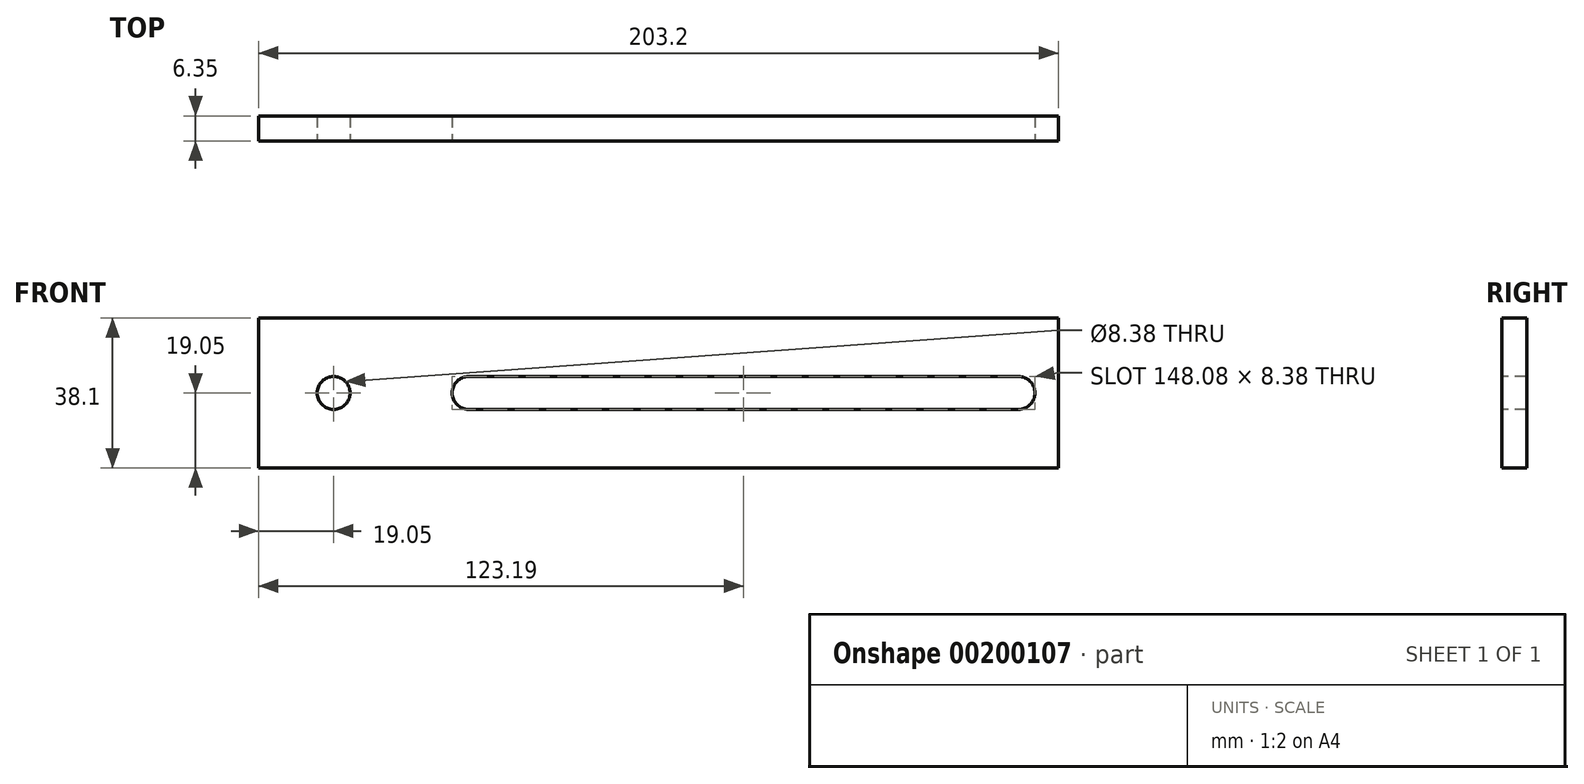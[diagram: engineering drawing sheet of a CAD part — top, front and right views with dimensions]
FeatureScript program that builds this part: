
annotation { "Feature Type Name" : "Feature", "Feature Type Description" : "" }
export const myFeature = defineFeature(function(context is Context, id is Id, definition is map)
    precondition{}
    {
        {
            var Q0;
            Q0=qCreatedBy(makeId("Front.planeOp"),FACE);
            var sketch = newSketch(context, id + "F0", { "sketchPlane" : qUnion([Q0])});
            skLineSegment(sketch, "E0.bottom", {"start": v(101.6, -19.05) * mm, "end": v(-101.6, -19.05) * mm});
            skLineSegment(sketch, "E0.top", {"start": v(101.6, 19.05) * mm, "end": v(-101.6, 19.05) * mm});
            skLineSegment(sketch, "E0.left", {"start": v(101.6, -19.05) * mm, "end": v(101.6, 19.05) * mm});
            skLineSegment(sketch, "E0.right", {"start": v(-101.6, -19.05) * mm, "end": v(-101.6, 19.05) * mm});
            skPoint(sketch, "E0.middle", {"position": v(0, 0) * mm});
            skSolve(sketch);
        }
        {
            var Q0;
            Q0=makeQuery(id+"F0.imprint","IMPRINT",FACE,{"disambiguationData":[TD([[makeQuery(id+"F0.imprint","IMPRINT",EDGE,{"derivedFrom":sQuery(id+"F0.wireOp",EDGE,"E0.bottom")}),-1.0]])]});
            extrude(context, id + "F1", {"entities" : qUnion([Q0]), "depth" : 6.35 * mm});
        }
        {
            var Q0;
            Q0=makeQuery(id+"F1.opExtrude","CAP_FACE",FACE,{"disambiguationData":[OSD([sQuery(id+"F0.wireOp",EDGE,"E0.bottom"),sQuery(id+"F0.wireOp",EDGE,"E0.top"),sQuery(id+"F0.wireOp",EDGE,"E0.left"),sQuery(id+"F0.wireOp",EDGE,"E0.right")])],"isStart":false});
            var sketch = newSketch(context, id + "F2", { "sketchPlane" : qUnion([Q0])});
            skPoint(sketch, "E1.endSnap0", {"position": v(-101.6, 0) * mm});
            skPoint(sketch, "E2", {"position": v(-82.55, 0) * mm});
            skCircle(sketch, "E3", {"center": v(-82.55, 0) * mm, "radius": 4.2 * mm});
            skSolve(sketch);
        }
        {
            var Q0;
            Q0=makeQuery(id+"F2.imprint","IMPRINT",FACE,{"disambiguationData":[TD([[makeQuery(id+"F2.imprint","IMPRINT",EDGE,{"derivedFrom":sQuery(id+"F2.wireOp",EDGE,"E3")}),1.0]])]});
            extrude(context, id + "F3", {"entities" : qUnion([Q0]), "operationType" : NewBodyOperationType.REMOVE, "endBound" : BoundingType.UP_TO_NEXT, "oppositeDirection" : true, "depth" : 25.4 * mm});
        }
        {
            var Q0;
            Q0=makeQuery(id+"F1.opExtrude","CAP_FACE",FACE,{"disambiguationData":[OSD([sQuery(id+"F0.wireOp",EDGE,"E0.bottom"),sQuery(id+"F0.wireOp",EDGE,"E0.top"),sQuery(id+"F0.wireOp",EDGE,"E0.left"),sQuery(id+"F0.wireOp",EDGE,"E0.right")])],"isStart":false});
            var sketch = newSketch(context, id + "F4", { "sketchPlane" : qUnion([Q0])});
            skLineSegment(sketch, "E4.bottom", {"start": v(91.44, -4.2) * mm, "end": v(-48.26, -4.2) * mm});
            skLineSegment(sketch, "E4.top", {"start": v(91.44, 4.2) * mm, "end": v(-48.26, 4.2) * mm});
            skLineSegment(sketch, "E4.left", {"start": v(91.44, -4.2) * mm, "end": v(91.44, 4.2) * mm});
            skLineSegment(sketch, "E4.right", {"start": v(-48.26, -4.2) * mm, "end": v(-48.26, 4.2) * mm});
            skPoint(sketch, "E4.middle", {"position": v(21.59, 0) * mm});
            skArc(sketch, "E5", {"start": v(-48.26, 4.2) * mm, "mid": v(-52.45, 0) * mm, "end": v(-48.26, -4.2) * mm});
            skArc(sketch, "E6", {"start": v(91.44, -4.2) * mm, "mid": v(95.63, 0) * mm, "end": v(91.44, 4.2) * mm});
            skSolve(sketch);
        }
        {
            var Q0;
            Q0=makeQuery(id+"F4.imprint","IMPRINT",FACE,{"disambiguationData":[TD([[makeQuery(id+"F4.imprint","IMPRINT",EDGE,{"derivedFrom":sQuery(id+"F4.wireOp",EDGE,"E4.bottom")}),-1.0]])]});
            var Q1;
            Q1=makeQuery(id+"F4.imprint","IMPRINT",FACE,{"disambiguationData":[TD([[makeQuery(id+"F4.imprint","IMPRINT",EDGE,{"derivedFrom":sQuery(id+"F4.wireOp",EDGE,"E4.left")}),-1.0]])]});
            var Q2;
            Q2=makeQuery(id+"F4.imprint","IMPRINT",FACE,{"disambiguationData":[TD([[makeQuery(id+"F4.imprint","IMPRINT",EDGE,{"derivedFrom":sQuery(id+"F4.wireOp",EDGE,"E4.right")}),1.0]])]});
            extrude(context, id + "F5", {"entities" : qUnion([Q0, Q1, Q2]), "operationType" : NewBodyOperationType.REMOVE, "oppositeDirection" : true, "depth" : 25.4 * mm});
        }
    });
